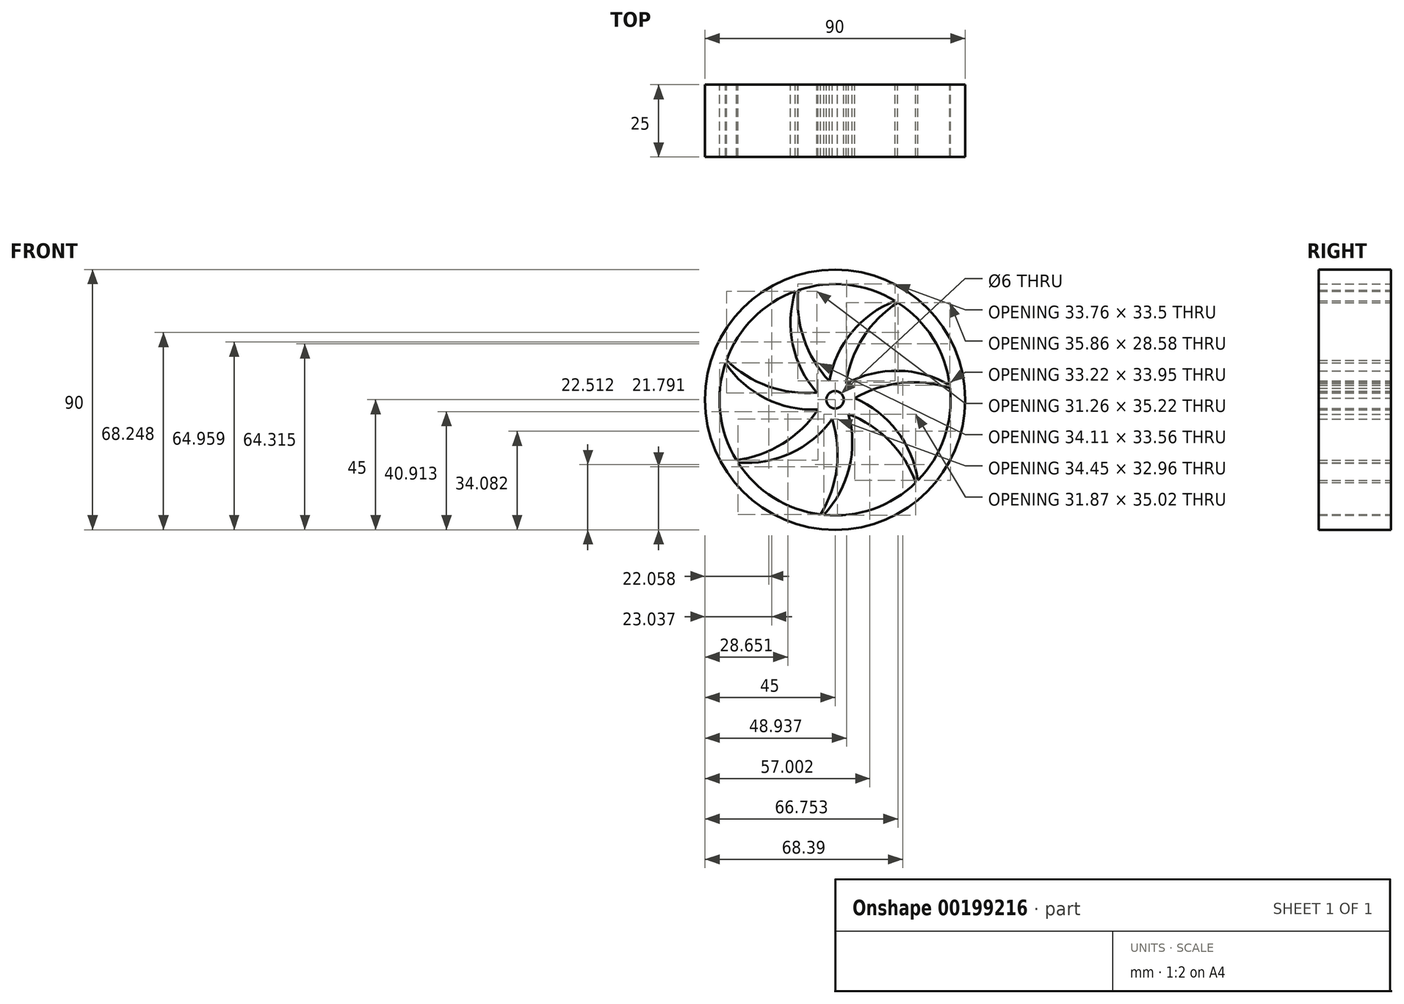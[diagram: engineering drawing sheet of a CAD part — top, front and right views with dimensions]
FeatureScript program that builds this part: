
annotation { "Feature Type Name" : "Feature", "Feature Type Description" : "" }
export const myFeature = defineFeature(function(context is Context, id is Id, definition is map)
    precondition{}
    {
        {
            var Q0;
            Q0=qCreatedBy(makeId("Front.planeOp"),FACE);
            var sketch = newSketch(context, id + "F0", { "sketchPlane" : qUnion([Q0])});
            skCircle(sketch, "E0", {"center": v(0, 0) * mm, "radius": 3 * mm});
            skArc(sketch, "E1", {"start": v(-2.46, 3.16) * mm, "mid": v(-0.78, -3.92) * mm, "end": v(3.48, 1.98) * mm});
            skCircle(sketch, "E2", {"center": v(0, 0) * mm, "radius": 40 * mm});
            skCircle(sketch, "E3", {"center": v(0, 0) * mm, "radius": 45 * mm});
            skPoint(sketch, "E4.first.point", {"position": v(3.48, 1.98) * mm});
            skArc(sketch, "E5.trimOffspring", {"start": v(21.7, 33.6) * mm, "mid": v(8.77, 19.99) * mm, "end": v(3.48, 1.98) * mm});
            skArc(sketch, "E6.trimOffspring", {"start": v(20.81, 34.16) * mm, "mid": v(4.74, 21.99) * mm, "end": v(-2.46, 3.16) * mm});
            skSolve(sketch);
        }
        {
            var Q0;
            Q0=makeQuery(id+"F0.imprint","IMPRINT",FACE,{"disambiguationData":[TD([[makeQuery(id+"F0.imprint","IMPRINT",EDGE,{"derivedFrom":sQuery(id+"F0.wireOp",EDGE,"E0")}),-1.0]])]});
            var Q1;
            {var subQ0=sQuery(id+"F0.wireOp",EDGE,"04f7a4a0-a9d0-4ee7-8d34-f135beb3edef");Q1=makeQuery(id+"F0.imprint","IMPRINT",FACE,{"disambiguationData":[TD([[makeQuery(id+"F0.imprint","IMPRINT",EDGE,{"derivedFrom":subQ0}),1.0]])]});}
            var Q2;
            Q2=makeQuery(id+"F0.imprint","IMPRINT",FACE,{"disambiguationData":[TD([[makeQuery(id+"F0.imprint","IMPRINT",EDGE,{"derivedFrom":sQuery(id+"F0.wireOp",EDGE,"E3")}),1.0]])]});
            extrude(context, id + "F1", {"entities" : qUnion([Q0, Q1, Q2]), "depth" : 25 * mm});
        }
        {
            var Q0;
            Q0=makeQuery(id+"F1.opExtrude","SWEPT_BODY",BODY,{"disambiguationData":[OSD([sQuery(id+"F0.wireOp",EDGE,"E0"),sQuery(id+"F0.wireOp",EDGE,"E1"),sQuery(id+"F0.wireOp",EDGE,"E2"),sQuery(id+"F0.wireOp",EDGE,"E3"),sQuery(id+"F0.wireOp",EDGE,"E4"),sQuery(id+"F0.wireOp",EDGE,"04f7a4a0-a9d0-4ee7-8d34-f135beb3edef")])]});
            var Q1;
            Q1=makeQuery(id+"F1.opExtrude","CAP_EDGE",EDGE,{"disambiguationData":[OSD([sQuery(id+"F0.wireOp",EDGE,"E0")])],"isStart":false});
            circularPattern(context, id + "F2", {"operationType" : NewBodyOperationType.ADD, "entities" : qUnion([Q0]), "axis" : qUnion([Q1]), "angle" : 360 * degree, "instanceCount" : 7, "equalSpace" : true, "computeTransformsWithoutBuiltin" : true});
        }
    });
